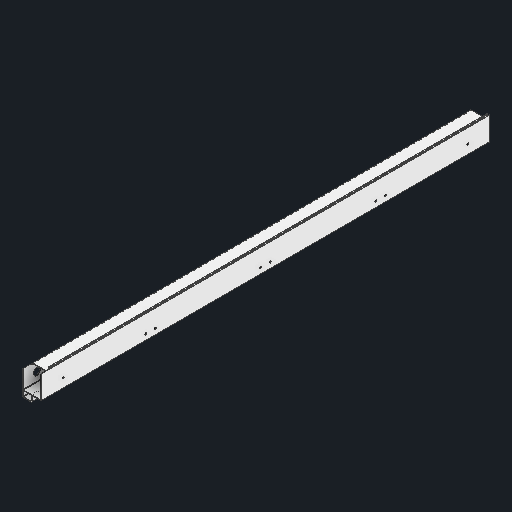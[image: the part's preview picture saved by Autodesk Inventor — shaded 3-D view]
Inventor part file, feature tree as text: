
AUTODESK INVENTOR PART (.ipt)
format: ipt  version: 2024.2 (Build 282272000, 272)  size: 154,624 bytes
history: native  units: in
note: dims shown in document units (in); Inventor stores cm internally (conversion verified against a paired STEP export)
features: fillet x1
ambient origin geometry x8: Origin, YZ Plane, XZ Plane, XY Plane, X Axis, Y Axis, Z Axis, Center Point
bodies: Solid1 (feature_tree)
feature tree (1):
  fillet  "Fillet6"  [1 undecoded]
note: 1 required parameter value undecoded (feature->parameter linkage not recoverable at this tier; creation-order binding heuristic only, values carry confidence <= 0.55)
